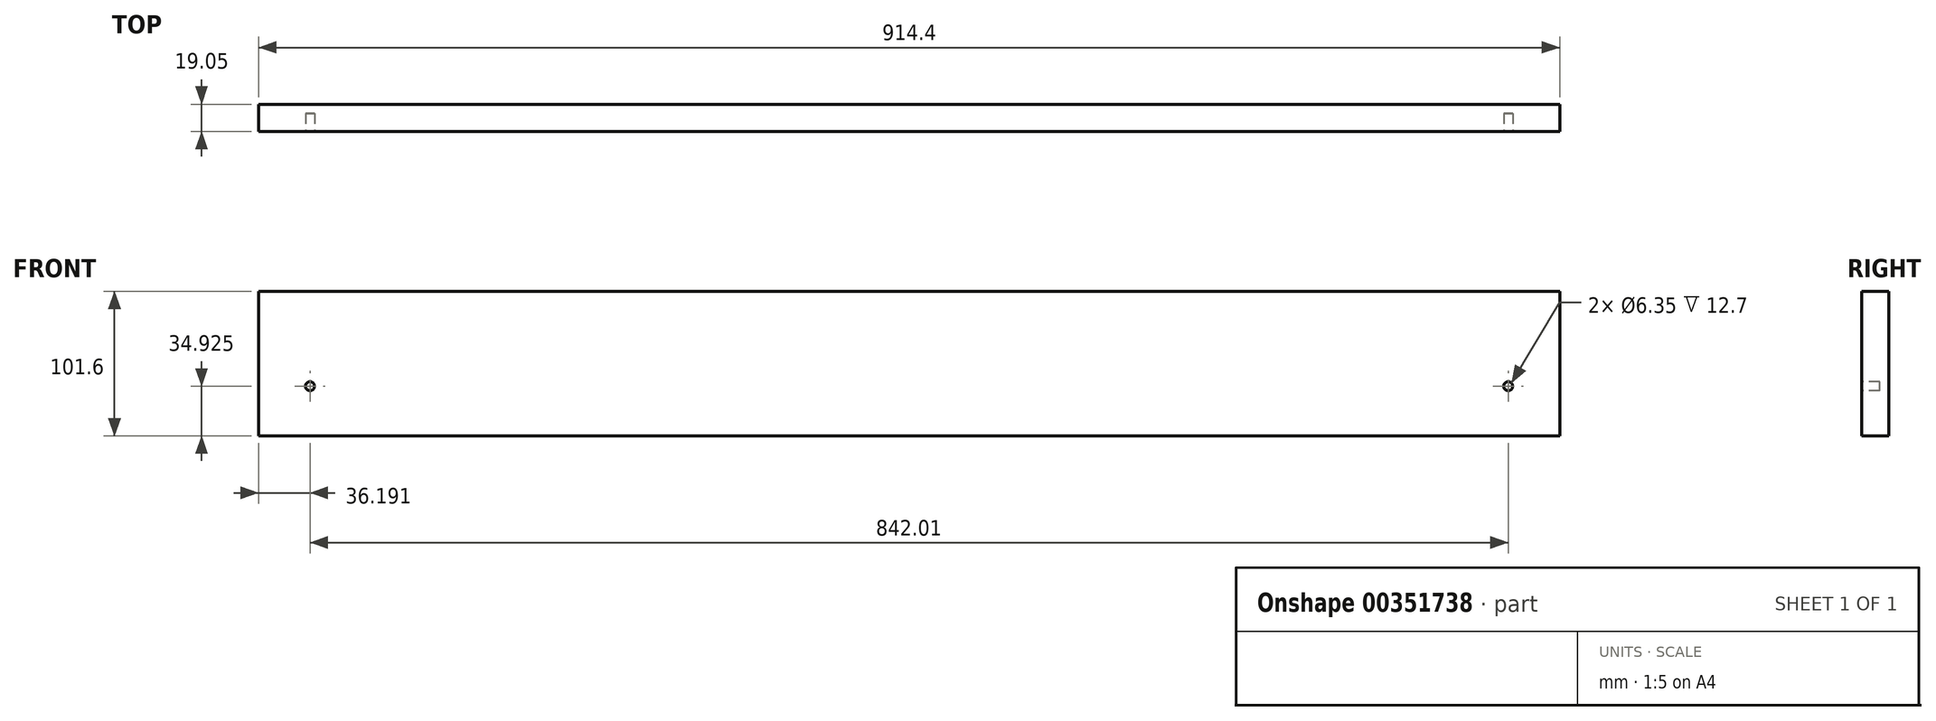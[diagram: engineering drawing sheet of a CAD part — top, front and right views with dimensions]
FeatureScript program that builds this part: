
annotation { "Feature Type Name" : "Feature", "Feature Type Description" : "" }
export const myFeature = defineFeature(function(context is Context, id is Id, definition is map)
    precondition{}
    {
        {
            var Q0;
            Q0=qCreatedBy(makeId("Front.planeOp"),FACE);
            var sketch = newSketch(context, id + "F0", { "sketchPlane" : qUnion([Q0])});
            skLineSegment(sketch, "E0.bottom", {"start": v(-461.9, 50.8) * mm, "end": v(452.5, 50.8) * mm});
            skLineSegment(sketch, "E0.top", {"start": v(-461.9, -50.8) * mm, "end": v(452.5, -50.8) * mm});
            skLineSegment(sketch, "E0.left", {"start": v(-461.9, 50.8) * mm, "end": v(-461.9, -50.8) * mm});
            skLineSegment(sketch, "E0.right", {"start": v(452.5, 50.8) * mm, "end": v(452.5, -50.8) * mm});
            skPoint(sketch, "E0.middle", {"position": v(-4.7, 0) * mm});
            skSolve(sketch);
        }
        {
            var Q0;
            Q0=makeQuery(id+"F0.imprint","IMPRINT",FACE,{"disambiguationData":[TD([[makeQuery(id+"F0.imprint","IMPRINT",EDGE,{"derivedFrom":sQuery(id+"F0.wireOp",EDGE,"E0.bottom")}),-1.0]])]});
            extrude(context, id + "F1", {"entities" : qUnion([Q0]), "depth" : 19.05 * mm});
        }
        {
            var Q0;
            Q0=makeQuery(id+"F1.opExtrude","CAP_FACE",FACE,{"disambiguationData":[OSD([sQuery(id+"F0.wireOp",EDGE,"E0.bottom"),sQuery(id+"F0.wireOp",EDGE,"E0.top"),sQuery(id+"F0.wireOp",EDGE,"E0.left"),sQuery(id+"F0.wireOp",EDGE,"E0.right")])],"isStart":false});
            var sketch = newSketch(context, id + "F2", { "sketchPlane" : qUnion([Q0])});
            skCircle(sketch, "E1", {"center": v(-425.7, -15.88) * mm, "radius": 3.18 * mm});
            skCircle(sketch, "E2", {"center": v(416.3, -15.87) * mm, "radius": 3.18 * mm});
            skSolve(sketch);
        }
        {
            var Q0;
            Q0=makeQuery(id+"F2.imprint","IMPRINT",FACE,{"disambiguationData":[TD([[makeQuery(id+"F2.imprint","IMPRINT",EDGE,{"derivedFrom":sQuery(id+"F2.wireOp",EDGE,"E2")}),1.0]])]});
            var Q1;
            Q1=makeQuery(id+"F2.imprint","IMPRINT",FACE,{"disambiguationData":[TD([[makeQuery(id+"F2.imprint","IMPRINT",EDGE,{"derivedFrom":sQuery(id+"F2.wireOp",EDGE,"E1")}),1.0]])]});
            extrude(context, id + "F3", {"entities" : qUnion([Q0, Q1]), "operationType" : NewBodyOperationType.REMOVE, "oppositeDirection" : true, "depth" : 12.7 * mm, "offsetDistance" : 25.4 * mm});
        }
    });
